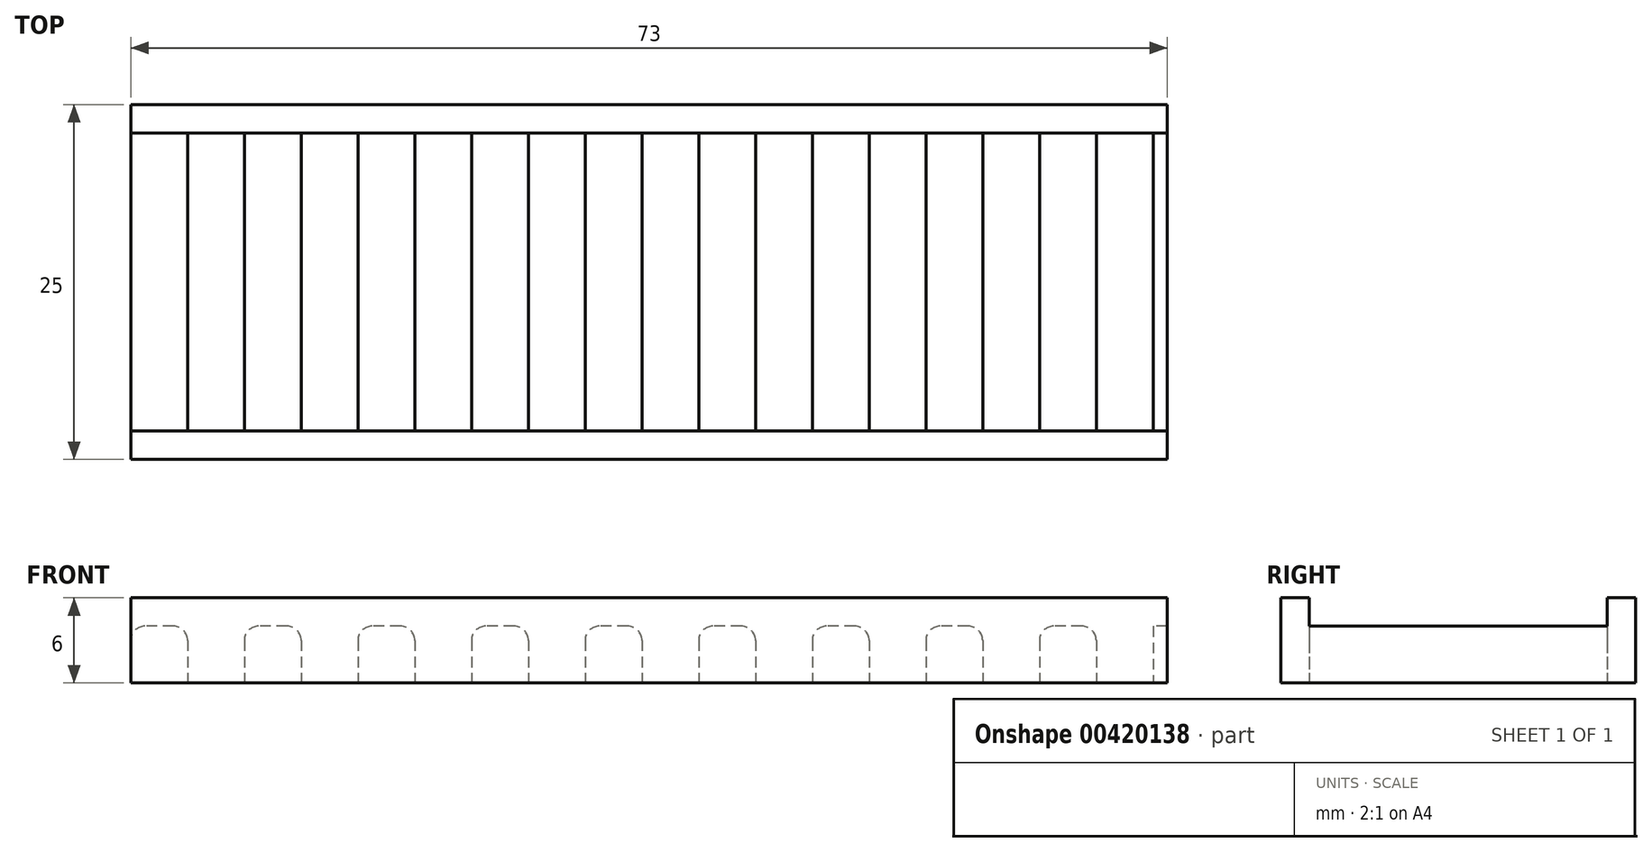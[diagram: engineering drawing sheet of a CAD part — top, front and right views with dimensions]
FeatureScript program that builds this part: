
annotation { "Feature Type Name" : "Feature", "Feature Type Description" : "" }
export const myFeature = defineFeature(function(context is Context, id is Id, definition is map)
    precondition{}
    {
        {
            var Q0;
            Q0=qCreatedBy(makeId("Top.planeOp"),FACE);
            var sketch = newSketch(context, id + "F0", { "sketchPlane" : qUnion([Q0])});
            skLineSegment(sketch, "E0", {"start": v(0, 0) * mm, "end": v(73, 0) * mm});
            skLineSegment(sketch, "E1", {"start": v(73, 0) * mm, "end": v(73, 25) * mm});
            skLineSegment(sketch, "E2", {"start": v(73, 25) * mm, "end": v(0, 25) * mm});
            skLineSegment(sketch, "E3", {"start": v(0, 25) * mm, "end": v(0, 0) * mm});
            skLineSegment(sketch, "E4.0", {"start": v(4, 23) * mm, "end": v(4, 2) * mm});
            skLineSegment(sketch, "E5.0", {"start": v(8, 23) * mm, "end": v(8, 2) * mm});
            skLineSegment(sketch, "E6.0", {"start": v(12, 23) * mm, "end": v(12, 2) * mm});
            skLineSegment(sketch, "E7.0", {"start": v(16, 23) * mm, "end": v(16, 2) * mm});
            skLineSegment(sketch, "E8.0", {"start": v(20, 23) * mm, "end": v(20, 2) * mm});
            skLineSegment(sketch, "E9.0", {"start": v(24, 23) * mm, "end": v(24, 2) * mm});
            skLineSegment(sketch, "E10.0", {"start": v(28, 23) * mm, "end": v(28, 2) * mm});
            skLineSegment(sketch, "E11.0", {"start": v(32, 23) * mm, "end": v(32, 2) * mm});
            skLineSegment(sketch, "E12.0", {"start": v(36, 23) * mm, "end": v(36, 2) * mm});
            skLineSegment(sketch, "E13.0", {"start": v(40, 23) * mm, "end": v(40, 2) * mm});
            skLineSegment(sketch, "E14.0", {"start": v(44, 23) * mm, "end": v(44, 2) * mm});
            skLineSegment(sketch, "E15.0", {"start": v(48, 23) * mm, "end": v(48, 2) * mm});
            skLineSegment(sketch, "E16.0", {"start": v(52, 23) * mm, "end": v(52, 2) * mm});
            skLineSegment(sketch, "E17.0", {"start": v(56, 23) * mm, "end": v(56, 2) * mm});
            skLineSegment(sketch, "E18.0", {"start": v(60, 23) * mm, "end": v(60, 2) * mm});
            skLineSegment(sketch, "E19.0", {"start": v(64, 23) * mm, "end": v(64, 2) * mm});
            skLineSegment(sketch, "E20.0", {"start": v(68, 25) * mm, "end": v(68, 2) * mm});
            skLineSegment(sketch, "E21.0", {"start": v(72, 23) * mm, "end": v(72, 2) * mm});
            skLineSegment(sketch, "E22.0", {"start": v(72, 23) * mm, "end": v(68, 23) * mm});
            skLineSegment(sketch, "E23.0", {"start": v(4, 2) * mm, "end": v(8, 2) * mm});
            skLineSegment(sketch, "E24.trimOffspring", {"start": v(64, 23) * mm, "end": v(60, 23) * mm});
            skLineSegment(sketch, "E25.trimOffspring", {"start": v(68, 2) * mm, "end": v(72, 2) * mm});
            skLineSegment(sketch, "E26.trimOffspring", {"start": v(60, 2) * mm, "end": v(64, 2) * mm});
            skLineSegment(sketch, "E27.trimOffspring", {"start": v(56, 23) * mm, "end": v(52, 23) * mm});
            skLineSegment(sketch, "E28.trimOffspring", {"start": v(48, 23) * mm, "end": v(44, 23) * mm});
            skLineSegment(sketch, "E29.trimOffspring", {"start": v(52, 2) * mm, "end": v(56, 2) * mm});
            skLineSegment(sketch, "E30.trimOffspring", {"start": v(44, 2) * mm, "end": v(48, 2) * mm});
            skLineSegment(sketch, "E31.trimOffspring", {"start": v(40, 23) * mm, "end": v(36, 23) * mm});
            skLineSegment(sketch, "E32.trimOffspring", {"start": v(32, 23) * mm, "end": v(28, 23) * mm});
            skLineSegment(sketch, "E33.trimOffspring", {"start": v(36, 2) * mm, "end": v(40, 2) * mm});
            skLineSegment(sketch, "E34.trimOffspring", {"start": v(28, 2) * mm, "end": v(32, 2) * mm});
            skLineSegment(sketch, "E35.trimOffspring", {"start": v(24, 23) * mm, "end": v(20, 23) * mm});
            skLineSegment(sketch, "E36.trimOffspring", {"start": v(16, 23) * mm, "end": v(12, 23) * mm});
            skLineSegment(sketch, "E37.trimOffspring", {"start": v(20, 2) * mm, "end": v(24, 2) * mm});
            skLineSegment(sketch, "E38.trimOffspring", {"start": v(12, 2) * mm, "end": v(16, 2) * mm});
            skLineSegment(sketch, "E39.trimOffspring", {"start": v(8, 23) * mm, "end": v(4, 23) * mm});
            skSolve(sketch);
        }
        {
            var Q0;
            Q0 = qSketchRegion(id + "F0", true);
            extrude(context, id + "F1", {"entities" : qUnion([Q0]), "depth" : 4 * mm});
        }
        {
            var Q0;
            Q0=makeQuery(id+"F1.opExtrude","CAP_EDGE",EDGE,{"disambiguationData":[OSD([sQuery(id+"F0.wireOp",EDGE,"E5.0")])],"isStart":false});
            var Q1;
            Q1=makeQuery(id+"F1.opExtrude","CAP_EDGE",EDGE,{"disambiguationData":[OSD([sQuery(id+"F0.wireOp",EDGE,"E6.0")])],"isStart":false});
            var Q2;
            Q2=makeQuery(id+"F1.opExtrude","CAP_EDGE",EDGE,{"disambiguationData":[OSD([sQuery(id+"F0.wireOp",EDGE,"E7.0")])],"isStart":false});
            var Q3;
            Q3=makeQuery(id+"F1.opExtrude","CAP_EDGE",EDGE,{"disambiguationData":[OSD([sQuery(id+"F0.wireOp",EDGE,"E8.0")])],"isStart":false});
            var Q4;
            Q4=makeQuery(id+"F1.opExtrude","CAP_EDGE",EDGE,{"disambiguationData":[OSD([sQuery(id+"F0.wireOp",EDGE,"E9.0")])],"isStart":false});
            var Q5;
            Q5=makeQuery(id+"F1.opExtrude","CAP_EDGE",EDGE,{"disambiguationData":[OSD([sQuery(id+"F0.wireOp",EDGE,"E10.0")])],"isStart":false});
            var Q6;
            Q6=makeQuery(id+"F1.opExtrude","CAP_EDGE",EDGE,{"disambiguationData":[OSD([sQuery(id+"F0.wireOp",EDGE,"E11.0")])],"isStart":false});
            var Q7;
            Q7=makeQuery(id+"F1.opExtrude","CAP_EDGE",EDGE,{"disambiguationData":[OSD([sQuery(id+"F0.wireOp",EDGE,"E12.0")])],"isStart":false});
            var Q8;
            Q8=makeQuery(id+"F1.opExtrude","CAP_EDGE",EDGE,{"disambiguationData":[OSD([sQuery(id+"F0.wireOp",EDGE,"E13.0")])],"isStart":false});
            var Q9;
            Q9=makeQuery(id+"F1.opExtrude","CAP_EDGE",EDGE,{"disambiguationData":[OSD([sQuery(id+"F0.wireOp",EDGE,"E14.0")])],"isStart":false});
            var Q10;
            Q10=makeQuery(id+"F1.opExtrude","CAP_EDGE",EDGE,{"disambiguationData":[OSD([sQuery(id+"F0.wireOp",EDGE,"E15.0")])],"isStart":false});
            var Q11;
            Q11=makeQuery(id+"F1.opExtrude","CAP_EDGE",EDGE,{"disambiguationData":[OSD([sQuery(id+"F0.wireOp",EDGE,"E16.0")])],"isStart":false});
            var Q12;
            Q12=makeQuery(id+"F1.opExtrude","CAP_EDGE",EDGE,{"disambiguationData":[OSD([sQuery(id+"F0.wireOp",EDGE,"E17.0")])],"isStart":false});
            var Q13;
            Q13=makeQuery(id+"F1.opExtrude","CAP_EDGE",EDGE,{"disambiguationData":[OSD([sQuery(id+"F0.wireOp",EDGE,"E18.0")])],"isStart":false});
            var Q14;
            Q14=makeQuery(id+"F1.opExtrude","CAP_EDGE",EDGE,{"disambiguationData":[OSD([sQuery(id+"F0.wireOp",EDGE,"E19.0")])],"isStart":false});
            var Q15;
            Q15=makeQuery(id+"F1.opExtrude","CAP_EDGE",EDGE,{"disambiguationData":[OSD([sQuery(id+"F0.wireOp",EDGE,"E20.0")])],"isStart":false});
            fillet(context, id + "F2", {"entities" : qUnion([Q0, Q1, Q2, Q3, Q4, Q5, Q6, Q7, Q8, Q9, Q10, Q11, Q12, Q13, Q14, Q15]), "radius" : 1 * mm, "tangentPropagation" : true, "allowEdgeOverflow" : false});
        }
        {
            var Q0;
            Q0=makeQuery(id+"F1.opExtrude","CAP_FACE",FACE,{"disambiguationData":[OSD([sQuery(id+"F0.wireOp",EDGE,"E0"),sQuery(id+"F0.wireOp",EDGE,"E1"),sQuery(id+"F0.wireOp",EDGE,"E2"),sQuery(id+"F0.wireOp",EDGE,"E3"),sQuery(id+"F0.wireOp",EDGE,"E4.0"),sQuery(id+"F0.wireOp",EDGE,"E5.0"),sQuery(id+"F0.wireOp",EDGE,"E6.0"),sQuery(id+"F0.wireOp",EDGE,"E7.0"),sQuery(id+"F0.wireOp",EDGE,"E8.0"),sQuery(id+"F0.wireOp",EDGE,"E9.0"),sQuery(id+"F0.wireOp",EDGE,"E10.0"),sQuery(id+"F0.wireOp",EDGE,"E11.0"),sQuery(id+"F0.wireOp",EDGE,"E12.0"),sQuery(id+"F0.wireOp",EDGE,"E13.0"),sQuery(id+"F0.wireOp",EDGE,"E14.0"),sQuery(id+"F0.wireOp",EDGE,"E15.0"),sQuery(id+"F0.wireOp",EDGE,"E16.0"),sQuery(id+"F0.wireOp",EDGE,"E17.0"),sQuery(id+"F0.wireOp",EDGE,"E18.0"),sQuery(id+"F0.wireOp",EDGE,"E19.0"),sQuery(id+"F0.wireOp",EDGE,"E20.0"),sQuery(id+"F0.wireOp",EDGE,"E21.0"),sQuery(id+"F0.wireOp",EDGE,"E22.0"),sQuery(id+"F0.wireOp",EDGE,"E23.0"),sQuery(id+"F0.wireOp",EDGE,"E24.trimOffspring"),sQuery(id+"F0.wireOp",EDGE,"E25.trimOffspring"),sQuery(id+"F0.wireOp",EDGE,"E26.trimOffspring"),sQuery(id+"F0.wireOp",EDGE,"E27.trimOffspring"),sQuery(id+"F0.wireOp",EDGE,"E28.trimOffspring"),sQuery(id+"F0.wireOp",EDGE,"E29.trimOffspring"),sQuery(id+"F0.wireOp",EDGE,"E30.trimOffspring"),sQuery(id+"F0.wireOp",EDGE,"E31.trimOffspring"),sQuery(id+"F0.wireOp",EDGE,"E32.trimOffspring"),sQuery(id+"F0.wireOp",EDGE,"E33.trimOffspring"),sQuery(id+"F0.wireOp",EDGE,"E34.trimOffspring"),sQuery(id+"F0.wireOp",EDGE,"E35.trimOffspring"),sQuery(id+"F0.wireOp",EDGE,"E36.trimOffspring"),sQuery(id+"F0.wireOp",EDGE,"E37.trimOffspring"),sQuery(id+"F0.wireOp",EDGE,"E38.trimOffspring"),sQuery(id+"F0.wireOp",EDGE,"E39.trimOffspring")])],"isStart":false});
            var sketch = newSketch(context, id + "F3", { "sketchPlane" : qUnion([Q0])});
            skLineSegment(sketch, "E40", {"start": v(73, 2) * mm, "end": v(0, 2) * mm});
            skLineSegment(sketch, "E41", {"start": v(73, 23) * mm, "end": v(0, 23) * mm});
            skLineSegment(sketch, "E42", {"start": v(0, 23) * mm, "end": v(0, 25) * mm});
            skLineSegment(sketch, "E43", {"start": v(0, 25) * mm, "end": v(73, 25) * mm});
            skLineSegment(sketch, "E44", {"start": v(73, 25) * mm, "end": v(73, 23) * mm});
            skLineSegment(sketch, "E45", {"start": v(0, 2) * mm, "end": v(0, 0) * mm});
            skLineSegment(sketch, "E46", {"start": v(0, 0) * mm, "end": v(73, 0) * mm});
            skLineSegment(sketch, "E47", {"start": v(73, 0) * mm, "end": v(73, 2) * mm});
            skSolve(sketch);
        }
        {
            var Q0;
            Q0 = qSketchRegion(id + "F3", true);
            extrude(context, id + "F4", {"entities" : qUnion([Q0]), "operationType" : NewBodyOperationType.ADD, "depth" : 2 * mm});
        }
        {
            var Q0;
            Q0=makeQuery(id+"F1.opExtrude","CAP_EDGE",EDGE,{"disambiguationData":[OSD([sQuery(id+"F0.wireOp",EDGE,"E4.0")])],"isStart":false});
            var Q1;
            Q1=makeQuery(id+"F1.opExtrude","CAP_EDGE",EDGE,{"disambiguationData":[OSD([sQuery(id+"F0.wireOp",EDGE,"E3")])],"isStart":false});
            fillet(context, id + "F5", {"entities" : qUnion([Q0, Q1]), "radius" : 1 * mm, "tangentPropagation" : true, "allowEdgeOverflow" : false});
        }
    });
